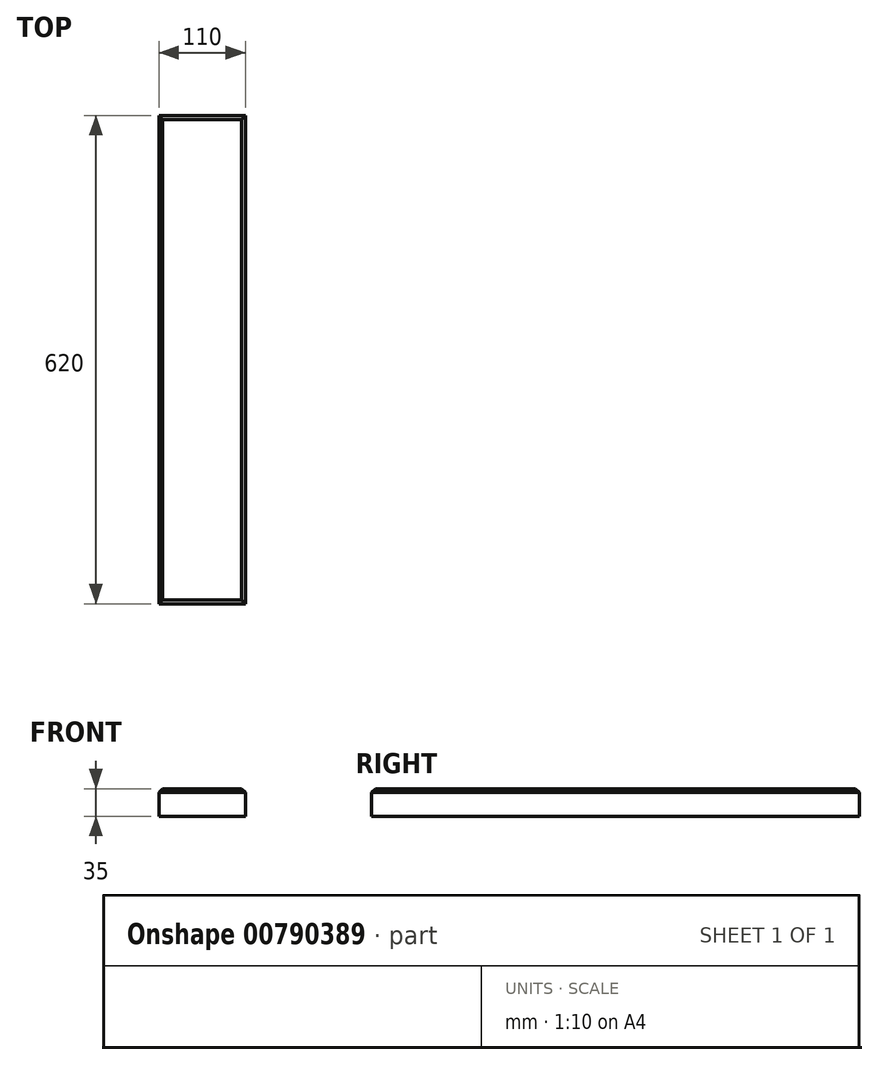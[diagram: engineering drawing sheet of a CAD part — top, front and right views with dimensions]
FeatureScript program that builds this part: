
annotation { "Feature Type Name" : "Feature", "Feature Type Description" : "" }
export const myFeature = defineFeature(function(context is Context, id is Id, definition is map)
    precondition{}
    {
        {
            assignVariable(context, id + "F0", {"name" : "OD80", "anyValue" : 35});
        }
        {
            var Q0;
            Q0=qCreatedBy(makeId("Top.planeOp"),FACE);
            var sketch = newSketch(context, id + "F1", { "sketchPlane" : qUnion([Q0])});
            skLineSegment(sketch, "E0.bottom", {"start": v(55, -310) * mm, "end": v(-55, -310) * mm});
            skLineSegment(sketch, "E0.top", {"start": v(55, 310) * mm, "end": v(-55, 310) * mm});
            skLineSegment(sketch, "E0.left", {"start": v(55, -310) * mm, "end": v(55, 310) * mm});
            skLineSegment(sketch, "E0.right", {"start": v(-55, -310) * mm, "end": v(-55, 310) * mm});
            skPoint(sketch, "E0.middle", {"position": v(0, 0) * mm});
            skPoint(sketch, "E1", {"position": v(-15, 240) * mm});
            skPoint(sketch, "E2", {"position": v(15, 240) * mm});
            skPoint(sketch, "E3", {"position": v(15, -240) * mm});
            skPoint(sketch, "E4", {"position": v(-15, -240) * mm});
            skSolve(sketch);
        }
        {
            var Q0;
            Q0=makeQuery(id+"F1.imprint","IMPRINT",FACE,{"disambiguationData":[TD([[makeQuery(id+"F1.imprint","IMPRINT",EDGE,{"derivedFrom":sQuery(id+"F1.wireOp",EDGE,"E0.bottom")}),-1.0]])]});
            extrude(context, id + "F2", {"entities" : qUnion([Q0]), "oppositeDirection" : true, "depth" : (getVariable(context, 'OD80')) * mm, "offsetDistance" : 25 * mm});
        }
        {
            var Q0;
            Q0=makeQuery(id+"F2.opExtrude","CAP_EDGE",EDGE,{"disambiguationData":[OSD([sQuery(id+"F1.wireOp",EDGE,"E0.right")])],"isStart":true});
            var Q1;
            Q1=makeQuery(id+"F2.opExtrude","CAP_EDGE",EDGE,{"disambiguationData":[OSD([sQuery(id+"F1.wireOp",EDGE,"E0.bottom")])],"isStart":true});
            var Q2;
            Q2=makeQuery(id+"F2.opExtrude","CAP_EDGE",EDGE,{"disambiguationData":[OSD([sQuery(id+"F1.wireOp",EDGE,"E0.left")])],"isStart":true});
            var Q3;
            Q3=makeQuery(id+"F2.opExtrude","CAP_EDGE",EDGE,{"disambiguationData":[OSD([sQuery(id+"F1.wireOp",EDGE,"E0.top")])],"isStart":true});
            chamfer(context, id + "F3", {"entities" : qUnion([Q0, Q1, Q2, Q3]), "width" : 5 * mm, "tangentPropagation" : true});
        }
    });
